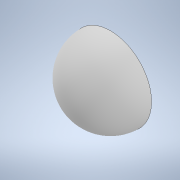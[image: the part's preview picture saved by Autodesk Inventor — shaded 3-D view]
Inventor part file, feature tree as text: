
AUTODESK INVENTOR PART (.ipt)
format: ipt  version: 2022 (Build 260153000, 153)  size: 126,464 bytes
history: native  units: in
note: dims shown in document units (in); Inventor stores cm internally (conversion verified against a paired STEP export)
features: sketch x2, revolve x1, extrude x1
ambient origin geometry x8: Origin, YZ Plane, XZ Plane, XY Plane, X Axis, Y Axis, Z Axis, Center Point
bodies: Solid2 (feature_tree)
feature tree (4):
  revolve  "Revolution1"  Angle=180.0deg
  extrude  "Extrusion3"  Depth=0.2in
  sketch  "Sketch1"  dims[d0=0.5in d1=180.0deg]
  sketch  "Sketch3"  dims[d5=0.06in d11=0.06in d12=0.06in d13=0.06in d14=0.2in d15=0.0in]
